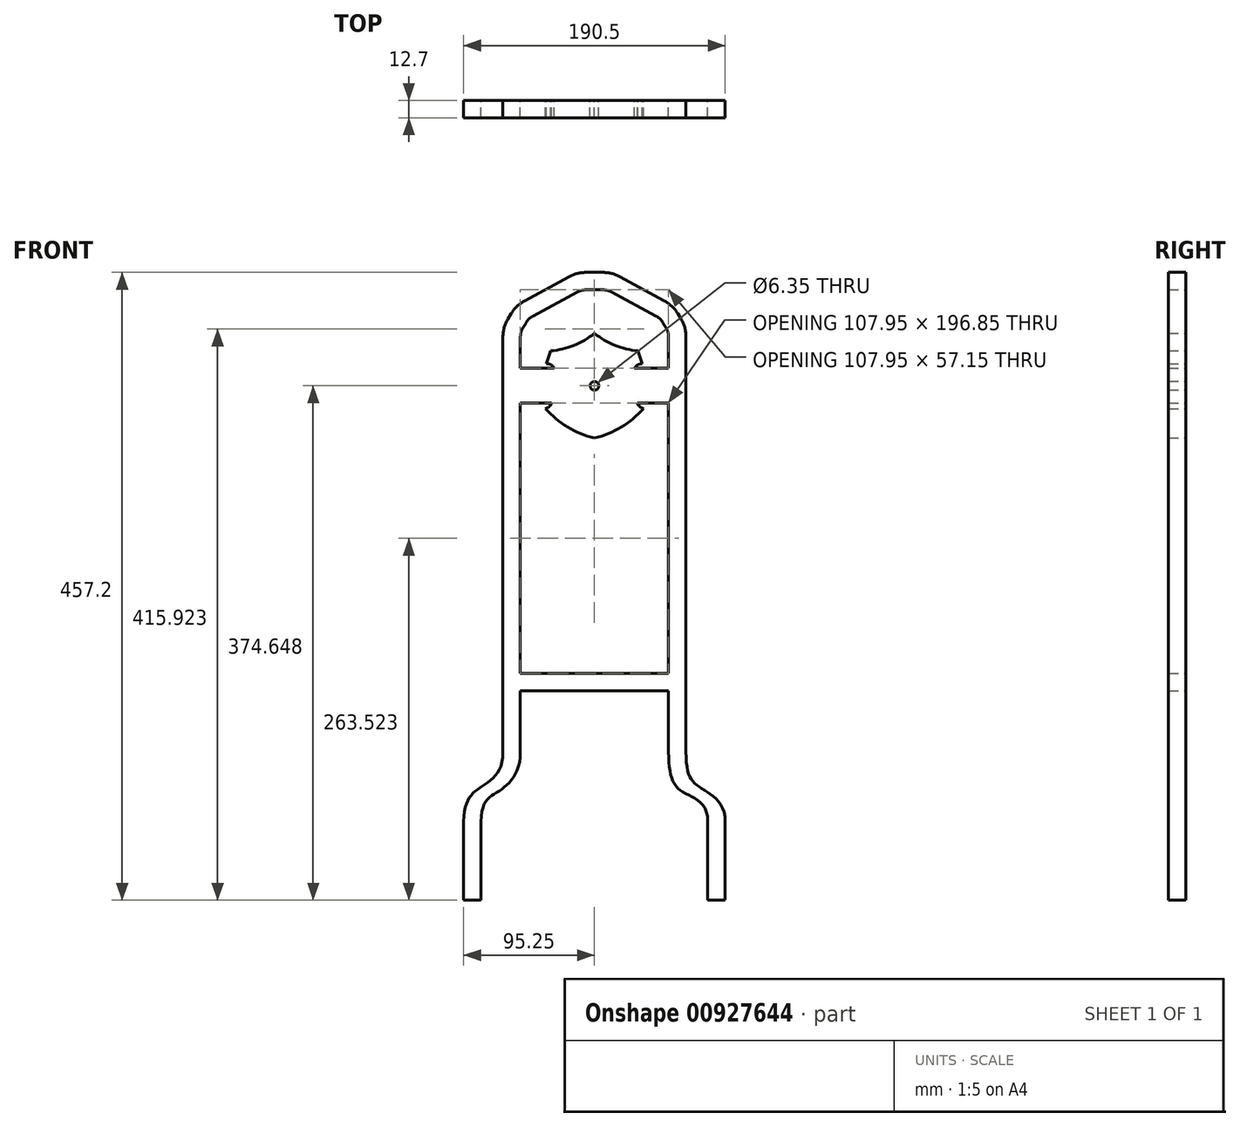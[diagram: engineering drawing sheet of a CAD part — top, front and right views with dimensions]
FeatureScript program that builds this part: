
annotation { "Feature Type Name" : "Feature", "Feature Type Description" : "" }
export const myFeature = defineFeature(function(context is Context, id is Id, definition is map)
    precondition{}
    {
        {
            var Q0;
            Q0=qCreatedBy(makeId("Front.planeOp"),FACE);
            var sketch = newSketch(context, id + "F0", { "sketchPlane" : qUnion([Q0])});
            skLineSegment(sketch, "E0", {"start": v(-95.25, -302.93) * mm, "end": v(-95.25, -245.78) * mm});
            skLineSegment(sketch, "E1", {"start": v(95.25, -302.93) * mm, "end": v(95.25, -245.78) * mm});
            skLineSegment(sketch, "E2", {"start": v(-66.67, 107.26) * mm, "end": v(-66.67, -194.98) * mm});
            skLineSegment(sketch, "E3", {"start": v(66.68, -194.98) * mm, "end": v(66.68, 107.26) * mm});
            skFitSpline(sketch, "E4", {"points": [v(-95.25, -245.78) * mm, v(-82.55, -220.38) * mm, v(-66.68, -194.98) * mm], "startDerivative": vector(0, 96.54) * mm, "endDerivative": vector(0, 94) * mm});
            skFitSpline(sketch, "E5", {"points": [v(66.68, -194.98) * mm, v(76.31, -220.38) * mm, v(95.25, -245.78) * mm], "startDerivative": vector(0, -99.06) * mm, "endDerivative": vector(0, -91.72) * mm});
            skLineSegment(sketch, "E6", {"start": v(-82.55, -302.93) * mm, "end": v(-82.55, -245.78) * mm});
            skFitSpline(sketch, "E7", {"points": [v(-82.55, -245.78) * mm, v(-69.85, -223.56) * mm, v(-53.98, -194.98) * mm], "startDerivative": vector(0, 101.44) * mm, "endDerivative": vector(0, 89.77) * mm});
            skLineSegment(sketch, "E8", {"start": v(-6.26, 154.27) * mm, "end": v(6.26, 154.27) * mm});
            skLineSegment(sketch, "E9", {"start": v(82.55, -302.93) * mm, "end": v(82.55, -245.78) * mm});
            skFitSpline(sketch, "E10", {"points": [v(53.98, -194.98) * mm, v(63.61, -223.56) * mm, v(82.55, -245.78) * mm], "startDerivative": vector(0, -94.49) * mm, "endDerivative": vector(0, -96.02) * mm});
            skLineSegment(sketch, "E11", {"start": v(-95.25, -302.93) * mm, "end": v(-82.55, -302.93) * mm});
            skLineSegment(sketch, "E12", {"start": v(82.55, -302.93) * mm, "end": v(95.25, -302.93) * mm});
            skLineSegment(sketch, "E13", {"start": v(-63.06, 120.33) * mm, "end": v(-60.72, 124.22) * mm});
            skLineSegment(sketch, "E14", {"start": v(-51.05, 133.48) * mm, "end": v(-18.36, 151.2) * mm});
            skLineSegment(sketch, "E15", {"start": v(18.36, 151.2) * mm, "end": v(51.05, 133.48) * mm});
            skLineSegment(sketch, "E16", {"start": v(60.72, 124.22) * mm, "end": v(63.06, 120.33) * mm});
            skPoint(sketch, "E17.visualSharp", {"position": v(-57.15, 130.17) * mm});
            skArc(sketch, "E17.filletArc", {"start": v(-51.05, 133.48) * mm, "mid": v(-56.5, 129.5) * mm, "end": v(-60.72, 124.22) * mm});
            skPoint(sketch, "E18.visualSharp", {"position": v(-66.67, 114.3) * mm});
            skArc(sketch, "E18.filletArc", {"start": v(-63.06, 120.33) * mm, "mid": v(-65.75, 114.04) * mm, "end": v(-66.68, 107.26) * mm});
            skPoint(sketch, "E19.visualSharp", {"position": v(-12.7, 154.27) * mm});
            skArc(sketch, "E19.filletArc", {"start": v(-6.26, 154.27) * mm, "mid": v(-12.5, 153.49) * mm, "end": v(-18.36, 151.2) * mm});
            skPoint(sketch, "E20.visualSharp", {"position": v(12.7, 154.27) * mm});
            skArc(sketch, "E20.filletArc", {"start": v(18.36, 151.2) * mm, "mid": v(12.5, 153.49) * mm, "end": v(6.26, 154.27) * mm});
            skPoint(sketch, "E21.visualSharp", {"position": v(57.15, 130.17) * mm});
            skArc(sketch, "E21.filletArc", {"start": v(60.72, 124.22) * mm, "mid": v(56.5, 129.5) * mm, "end": v(51.05, 133.48) * mm});
            skPoint(sketch, "E22.visualSharp", {"position": v(66.68, 114.3) * mm});
            skArc(sketch, "E22.filletArc", {"start": v(66.67, 107.26) * mm, "mid": v(65.75, 114.04) * mm, "end": v(63.06, 120.33) * mm});
            skArc(sketch, "E23.0", {"start": v(-52.17, 113.8) * mm, "mid": v(-53.51, 110.65) * mm, "end": v(-53.98, 107.26) * mm});
            skLineSegment(sketch, "E23.1", {"start": v(12.31, 140.03) * mm, "end": v(45, 122.32) * mm});
            skArc(sketch, "E23.2", {"start": v(49.83, 117.69) * mm, "mid": v(47.72, 120.33) * mm, "end": v(45, 122.32) * mm});
            skLineSegment(sketch, "E23.3", {"start": v(49.83, 117.69) * mm, "end": v(52.17, 113.8) * mm});
            skArc(sketch, "E23.4", {"start": v(53.98, 107.26) * mm, "mid": v(53.51, 110.65) * mm, "end": v(52.17, 113.8) * mm});
            skArc(sketch, "E23.5", {"start": v(12.31, 140.03) * mm, "mid": v(9.38, 141.18) * mm, "end": v(6.26, 141.57) * mm});
            skLineSegment(sketch, "E23.6", {"start": v(-6.26, 141.57) * mm, "end": v(6.26, 141.57) * mm});
            skArc(sketch, "E23.7", {"start": v(-6.26, 141.57) * mm, "mid": v(-9.38, 141.18) * mm, "end": v(-12.31, 140.03) * mm});
            skLineSegment(sketch, "E23.8", {"start": v(-45, 122.32) * mm, "end": v(-12.31, 140.03) * mm});
            skArc(sketch, "E23.9", {"start": v(-45, 122.32) * mm, "mid": v(-47.72, 120.33) * mm, "end": v(-49.83, 117.69) * mm});
            skLineSegment(sketch, "E23.10", {"start": v(-52.17, 113.8) * mm, "end": v(-49.83, 117.69) * mm});
            skArc(sketch, "E24", {"start": v(-31.75, 97.12) * mm, "mid": v(-14.96, 101.19) * mm, "end": v(0, 109.82) * mm});
            skArc(sketch, "E25", {"start": v(0, 109.82) * mm, "mid": v(14.96, 101.19) * mm, "end": v(31.75, 97.12) * mm});
            skArc(sketch, "E26", {"start": v(-29.2, 84.42) * mm, "mid": v(-31.5, 87.01) * mm, "end": v(-34.93, 87.6) * mm});
            skArc(sketch, "E27", {"start": v(34.93, 87.6) * mm, "mid": v(31.5, 87.01) * mm, "end": v(29.2, 84.42) * mm});
            skLineSegment(sketch, "E28", {"start": v(31.75, 97.12) * mm, "end": v(34.92, 87.6) * mm});
            skLineSegment(sketch, "E29", {"start": v(-31.75, 97.12) * mm, "end": v(-34.93, 87.6) * mm});
            skLineSegment(sketch, "E30", {"start": v(-29.21, 84.42) * mm, "end": v(-53.98, 84.42) * mm});
            skLineSegment(sketch, "E31", {"start": v(29.21, 84.42) * mm, "end": v(53.98, 84.42) * mm});
            skArc(sketch, "E32", {"start": v(31.22, 59.02) * mm, "mid": v(33, 56.55) * mm, "end": v(35.71, 55.17) * mm});
            skArc(sketch, "E33", {"start": v(-35.71, 55.17) * mm, "mid": v(-33, 56.55) * mm, "end": v(-31.22, 59.02) * mm});
            skLineSegment(sketch, "E34", {"start": v(-31.22, 59.02) * mm, "end": v(-53.98, 59.02) * mm});
            skLineSegment(sketch, "E35", {"start": v(31.22, 59.02) * mm, "end": v(53.97, 59.02) * mm});
            skArc(sketch, "E36", {"start": v(-35.71, 55.17) * mm, "mid": v(-19.54, 41.61) * mm, "end": v(0, 33.62) * mm});
            skArc(sketch, "E37", {"start": v(0, 33.62) * mm, "mid": v(19.54, 41.61) * mm, "end": v(35.71, 55.17) * mm});
            skLineSegment(sketch, "E38", {"start": v(-53.98, -194.98) * mm, "end": v(-53.98, 59.02) * mm});
            skLineSegment(sketch, "E39", {"start": v(-53.98, 84.42) * mm, "end": v(-53.98, 107.26) * mm});
            skLineSegment(sketch, "E40", {"start": v(53.98, 107.26) * mm, "end": v(53.98, 84.42) * mm});
            skLineSegment(sketch, "E41", {"start": v(53.98, 59.02) * mm, "end": v(53.98, -194.98) * mm});
            skCircle(sketch, "E42", {"center": v(0, 71.72) * mm, "radius": 3.18 * mm});
            skLineSegment(sketch, "E43.bottom", {"start": v(-53.98, -150.53) * mm, "end": v(53.98, -150.53) * mm});
            skLineSegment(sketch, "E43.top", {"start": v(-53.98, -137.83) * mm, "end": v(53.98, -137.83) * mm});
            skLineSegment(sketch, "E43.left", {"start": v(-53.98, -150.53) * mm, "end": v(-53.98, -137.83) * mm});
            skLineSegment(sketch, "E43.right", {"start": v(53.98, -150.53) * mm, "end": v(53.98, -137.83) * mm});
            skSolve(sketch);
        }
        {
            var Q0;
            Q0=makeQuery(id+"F0.imprint","IMPRINT",FACE,{"disambiguationData":[TD([[makeQuery(id+"F0.imprint","IMPRINT",EDGE,{"derivedFrom":sQuery(id+"F0.wireOp",EDGE,"E0")}),-1.0]])]});
            extrude(context, id + "F1", {"entities" : qUnion([Q0]), "depth" : 12.7 * mm, "offsetDistance" : 25.4 * mm});
        }
        {
            var Q0;
            Q0=makeQuery(id+"F0.imprint","IMPRINT",FACE,{"disambiguationData":[TD([[makeQuery(id+"F0.imprint","IMPRINT",EDGE,{"derivedFrom":sQuery(id+"F0.wireOp",EDGE,"E43.bottom")}),1.0]])]});
            extrude(context, id + "F2", {"entities" : qUnion([Q0]), "operationType" : NewBodyOperationType.ADD, "depth" : 12.7 * mm, "offsetDistance" : 25.4 * mm});
        }
    });
